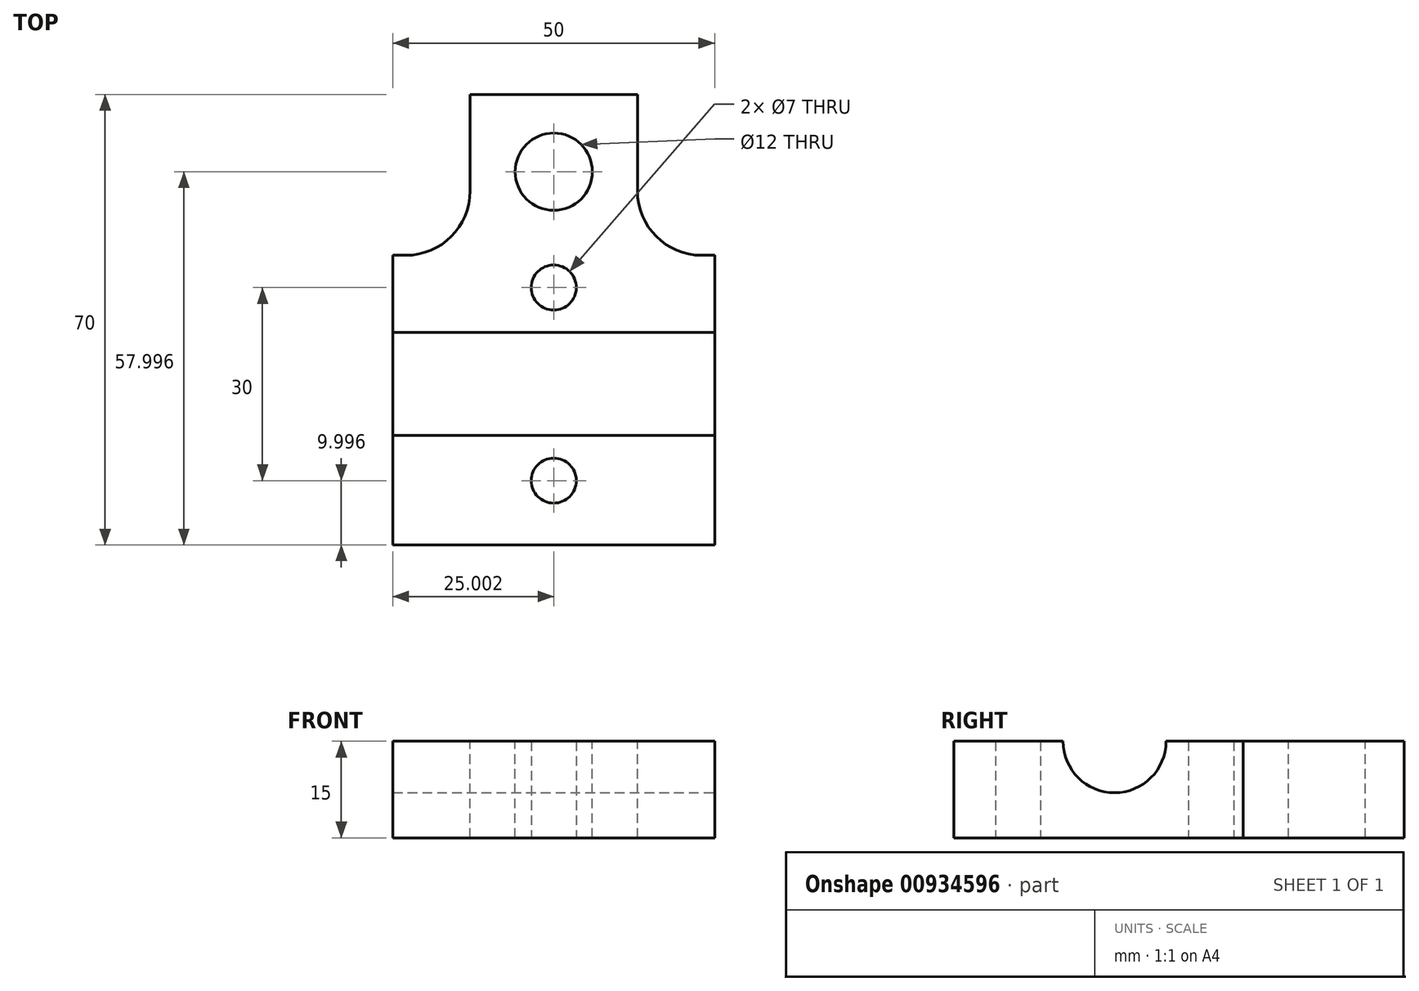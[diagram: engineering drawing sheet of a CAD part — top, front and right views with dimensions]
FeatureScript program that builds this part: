
annotation { "Feature Type Name" : "Feature", "Feature Type Description" : "" }
export const myFeature = defineFeature(function(context is Context, id is Id, definition is map)
    precondition{}
    {
        {
            var Q0;
            Q0=qCreatedBy(makeId("Top.planeOp"),FACE);
            var sketch = newSketch(context, id + "F0", { "sketchPlane" : qUnion([Q0])});
            skLineSegment(sketch, "E0.bottom", {"start": v(-18.79, -13.36) * mm, "end": v(31.21, -13.36) * mm});
            skLineSegment(sketch, "E0.top", {"start": v(-18.79, -83.36) * mm, "end": v(31.21, -83.36) * mm});
            skLineSegment(sketch, "E0.left", {"start": v(-18.79, -13.36) * mm, "end": v(-18.79, -83.36) * mm});
            skLineSegment(sketch, "E0.right", {"start": v(31.21, -13.36) * mm, "end": v(31.21, -83.36) * mm});
            skSolve(sketch);
        }
        {
            var Q0;
            Q0=qSketchRegion(id+"F0",true);
            extrude(context, id + "F1", {"entities" : qUnion([Q0]), "depth" : 15 * mm, "offsetDistance" : 25 * mm});
        }
        {
            var Q0;
            Q0=makeQuery(id+"F1.opExtrude","CAP_FACE",FACE,{"disambiguationData":[OSD([sQuery(id+"F0.wireOp",EDGE,"E0.bottom"),sQuery(id+"F0.wireOp",EDGE,"E0.top"),sQuery(id+"F0.wireOp",EDGE,"E0.left"),sQuery(id+"F0.wireOp",EDGE,"E0.right")])],"isStart":false});
            var sketch = newSketch(context, id + "F2", { "sketchPlane" : qUnion([Q0])});
            skCircle(sketch, "E1", {"center": v(6.21, -25.36) * mm, "radius": 6 * mm});
            skSolve(sketch);
        }
        {
            var Q0;
            Q0=qSketchRegion(id+"F2",true);
            extrude(context, id + "F3", {"entities" : qUnion([Q0]), "operationType" : NewBodyOperationType.REMOVE, "oppositeDirection" : true, "depth" : 25 * mm, "offsetDistance" : 25 * mm});
        }
        {
            var Q0;
            Q0=makeQuery(id+"F1.opExtrude","SWEPT_FACE",FACE,{"disambiguationData":[OSD([sQuery(id+"F0.wireOp",EDGE,"E0.right")])]});
            var sketch = newSketch(context, id + "F4", { "sketchPlane" : qUnion([Q0])});
            skCircle(sketch, "E2", {"center": v(-58.36, 15) * mm, "radius": 8 * mm});
            skSolve(sketch);
        }
        {
            var Q0;
            Q0=qSketchRegion(id+"F4",true);
            extrude(context, id + "F5", {"entities" : qUnion([Q0]), "operationType" : NewBodyOperationType.REMOVE, "endBound" : BoundingType.THROUGH_ALL, "oppositeDirection" : true, "depth" : 25 * mm, "offsetDistance" : 25 * mm});
        }
        {
            var Q0;
            Q0=makeQuery(id+"F1.opExtrude","CAP_FACE",FACE,{"disambiguationData":[OSD([sQuery(id+"F0.wireOp",EDGE,"E0.bottom"),sQuery(id+"F0.wireOp",EDGE,"E0.top"),sQuery(id+"F0.wireOp",EDGE,"E0.left"),sQuery(id+"F0.wireOp",EDGE,"E0.right")])],"isStart":true});
            var sketch = newSketch(context, id + "F6", { "sketchPlane" : qUnion([Q0])});
            skLineSegment(sketch, "E3", {"start": v(6.21, 25.36) * mm, "end": v(6.21, 73.36) * mm, "construction": true});
            skCircle(sketch, "E4", {"center": v(6.21, 73.36) * mm, "radius": 3.5 * mm});
            skCircle(sketch, "E5", {"center": v(6.21, 43.36) * mm, "radius": 3.5 * mm});
            skSolve(sketch);
        }
        {
            var Q0;
            Q0=makeQuery(id+"F6.imprint","IMPRINT",FACE,{"disambiguationData":[TD([[makeQuery(id+"F6.imprint","IMPRINT",EDGE,{"derivedFrom":sQuery(id+"F6.wireOp",EDGE,"E5")}),1.0]])]});
            var Q1;
            Q1=makeQuery(id+"F6.imprint","IMPRINT",FACE,{"disambiguationData":[TD([[makeQuery(id+"F6.imprint","IMPRINT",EDGE,{"derivedFrom":sQuery(id+"F6.wireOp",EDGE,"DmRhdCVF-GiDt-GYaT-hILc-mG9uuN7Jt7s4")}),1.0]])]});
            var Q2;
            Q2=makeQuery(id+"F6.imprint","IMPRINT",FACE,{"disambiguationData":[TD([[makeQuery(id+"F6.imprint","IMPRINT",EDGE,{"derivedFrom":sQuery(id+"F6.wireOp",EDGE,"E4")}),1.0]])]});
            extrude(context, id + "F7", {"entities" : qUnion([Q0, Q1, Q2]), "operationType" : NewBodyOperationType.REMOVE, "endBound" : BoundingType.THROUGH_ALL, "oppositeDirection" : true, "depth" : 25 * mm, "offsetDistance" : 25 * mm});
        }
        {
            var Q0;
            {var subQ0=sQuery(id+"F0.wireOp",EDGE,"E0.right");var subQ1=sQuery(id+"F0.wireOp",EDGE,"E0.left");var subQ2=sQuery(id+"F0.wireOp",EDGE,"E0.bottom");Q0=makeQuery(id+"F5.boolean.opBoolean","SPLIT",FACE,{"disambiguationData":[TD([makeQuery(id+"F1.opExtrude","SWEPT_FACE",FACE,{"disambiguationData":[OSD([subQ2])]})])],"derivedFrom":makeQuery(id+"F1.opExtrude","CAP_FACE",FACE,{"disambiguationData":[OSD([subQ2,sQuery(id+"F0.wireOp",EDGE,"E0.top"),subQ1,subQ0])],"isStart":false})});}
            var sketch = newSketch(context, id + "F8", { "sketchPlane" : qUnion([Q0])});
            skLineSegment(sketch, "E6.bottom", {"start": v(31.21, -13.36) * mm, "end": v(19.21, -13.36) * mm});
            skLineSegment(sketch, "E6.top", {"start": v(31.21, -38.36) * mm, "end": v(19.21, -38.36) * mm});
            skLineSegment(sketch, "E6.left", {"start": v(31.21, -13.36) * mm, "end": v(31.21, -38.36) * mm});
            skLineSegment(sketch, "E6.right", {"start": v(19.21, -13.36) * mm, "end": v(19.21, -38.36) * mm});
            skLineSegment(sketch, "E7.bottom", {"start": v(-18.79, -13.36) * mm, "end": v(-6.79, -13.36) * mm});
            skLineSegment(sketch, "E7.top", {"start": v(-18.79, -38.36) * mm, "end": v(-6.79, -38.36) * mm});
            skLineSegment(sketch, "E7.left", {"start": v(-18.79, -13.36) * mm, "end": v(-18.79, -38.36) * mm});
            skLineSegment(sketch, "E7.right", {"start": v(-6.79, -13.36) * mm, "end": v(-6.79, -38.36) * mm});
            skSolve(sketch);
        }
        {
            var Q0;
            Q0=makeQuery(id+"F8.imprint","IMPRINT",FACE,{"disambiguationData":[TD([[makeQuery(id+"F8.imprint","IMPRINT",EDGE,{"derivedFrom":sQuery(id+"F8.wireOp",EDGE,"E6.bottom")}),-1.0]])]});
            var Q1;
            Q1=makeQuery(id+"F8.imprint","IMPRINT",FACE,{"disambiguationData":[TD([[makeQuery(id+"F8.imprint","IMPRINT",EDGE,{"derivedFrom":sQuery(id+"F8.wireOp",EDGE,"E7.bottom")}),-1.0]])]});
            extrude(context, id + "F9", {"entities" : qUnion([Q0, Q1]), "operationType" : NewBodyOperationType.REMOVE, "endBound" : BoundingType.UP_TO_NEXT, "oppositeDirection" : true, "depth" : 25 * mm, "offsetDistance" : 25 * mm});
        }
        {
            var Q0;
            Q0=makeQuery(id+"F9.boolean.opBoolean","COPY",EDGE,{"derivedFrom":makeQuery(id+"F9.opExtrude","SWEPT_EDGE",EDGE,{"disambiguationData":[OSD([sQuery(id+"F0.wireOp",EDGE,"E0.bottom"),sQuery(id+"F8.wireOp",EDGE,"E6.bottom"),sQuery(id+"F8.wireOp",EDGE,"E6.right")])]})});
            var Q1;
            Q1=makeQuery(id+"F9.boolean.opBoolean","COPY",EDGE,{"derivedFrom":makeQuery(id+"F9.opExtrude","SWEPT_EDGE",EDGE,{"disambiguationData":[OSD([sQuery(id+"F0.wireOp",EDGE,"E0.bottom"),sQuery(id+"F8.wireOp",EDGE,"E7.bottom"),sQuery(id+"F8.wireOp",EDGE,"E7.right")])]})});
            var Q2;
            Q2=makeQuery(id+"F9.boolean.opBoolean","COPY",EDGE,{"derivedFrom":makeQuery(id+"F9.opExtrude","SWEPT_EDGE",EDGE,{"disambiguationData":[OSD([sQuery(id+"F8.wireOp",EDGE,"E7.top"),sQuery(id+"F8.wireOp",EDGE,"E7.right")])]})});
            var Q3;
            Q3=makeQuery(id+"F9.boolean.opBoolean","COPY",EDGE,{"derivedFrom":makeQuery(id+"F9.opExtrude","SWEPT_EDGE",EDGE,{"disambiguationData":[OSD([sQuery(id+"F8.wireOp",EDGE,"E6.top"),sQuery(id+"F8.wireOp",EDGE,"E6.right")])]})});
            fillet(context, id + "F10", {"entities" : qUnion([Q0, Q1, Q2, Q3]), "radius" : 10 * mm, "tangentPropagation" : true, "allowEdgeOverflow" : false});
        }
    });
